# Revit family: Metered PDU 1U
name_source: partatom
category: Installations électriques
units: mm (PartAtom-declared; Revit-internal decimal feet)

## family parameters
Basée sur le plan de construction = Non
Conserver l'orientation des annotations = Non
Cote de connecteur circulaire = Utiliser le diamètre
Couper avec des vides une fois chargée = Non
Numéro OmniClass = 23.80.00.00
Partagée = Non
Point de calcul de pièce = Non
Titre OmniClass = Electric Power and Lighting
Toujours verticalement = Oui
Type d'élément = Normal

## types (2) — shared parameters
Application class = EC002762
BIM wording = Linkeo DATA CENTER BASIC PDU
Color = Black
Connectable by internet box = Oui
Depth (mm) = 115 mm  [stored 0.377297 ft]
Description = PDU metered base 19 inch 1 phase 16A 12 C13 locking outlets IEC-320 C20
E-catalogue link = https://www.legrand.fr
Elévation par défaut = 1000 mm  [stored 3.28084 ft]
Fabricant = LEGRAND
Function = Unit DE DISTRIBUTION D'ENERGIE
IP = IP40
Length = 45 mm
Mounting direction = Horizontal
Number of C13 outlets = 8
Number of phases = 1
Power frequency = 50-50
Profondeur cuve + capot = 115 mm  [stored 0.377297 ft]
Programming way = Appli Web
RAL Number = 9017
Standby consumption = 0 mA
Supply current = 16-16
Terminal marking indication = Non
Type of electric connection = C20
Width (mm) = 483 mm
type of voltage = AC
zero-valued in all types: Number of C19 outlets, Number of MCB

## per-type parameters (varying)
| type | Base_Node | GTIN | Legrand part number |
| PDU MB 19P 1P 16A 12 C13 | Base_Node_Horizontal : Base HD | 3414972245852 | LG-646100 |
| PDU MN 19P 1P 16A 12 C13 | Base_Node_Horizontal : Node HD | 3414972245913 | LG-646101 |

note: [stored X ft] marks values corroborated as IEEE doubles in the binary element streams (Revit-internal decimal feet)
